# Revit family: Kessel 20223 en
name_source: partatom
category: Sanitärinstallationen
revit_build: Autodesk Revit 2017 (Build: 20160225_1515(x64)
units: mm (PartAtom-declared; Revit-internal decimal feet)

## family parameters
Arbeitsebenenbasiert = Nein
Beim Laden mit Abzugskörper schneiden = Nein
Bemaßung runder Anschluss = Durchmesser verwenden
Gemeinsam genutzt = Nein
Immer vertikal = Ja
Raumberechnungspunkt = Nein
Teiletyp = Normal

## types (1)
- Kessel 20223 en
    <1.010.00.2> Number of the part of the guideline = 4
    <1.010.00.3> Issue date (month) of the guideline = 201410
    <1.010.00.4> Manufacturer name = Kessel
    <1.010.00.5> Revision date of the file = 20190228
    <1.800.00.3> BS number = 10000100000000000000000000000000000000000000000102000
    <1.800.00.4> Comment field = Warngerät mit optischer Sonde
    <1.810.00.3> Manufacturer’s reference number = 20223
    <1.810.00.4> DATANORM number = 20223
    <1.960/3L.00.8> Link (URL) = http://www.kessel.de
    <4.100.00.4> Area of application = Zubehör
    <4.110.00.4> Model series = Zubehör
    <4.700.00.10> Star / delta starting circuit with three-phase connection or three-phase current = no
    <4.700.00.46> vertical installation = no
    <4.700.00.47> outdoor installation = no
    <4.700.00.48> ATEX = no
    <4.700.00.49> protection class = protection class I
    <4.700.00.4> Product name = Warngerät mit optischer Sonde
    <4.700.00.50> motor protection = no
    CONNECTOR0_DIAMETER_dZ_0r = 0 mm  [stored 0 ft]
    CONNECTOR0_dZ_00 = 77 mm
    CONNECTOR0_dZ_01 = 67 mm
    CONNECTOR0_ref_dX = 48 mm
    CONNECTOR0_ref_dY = 22 mm
    CONNECTOR0_ref_dZ = 67 mm
    CONNECTOR1_DIAMETER_dNBN0_0r = 0 mm  [stored 0 ft]
    CONNECTOR1_dNBN0_00 = 76 mm
    CONNECTOR1_dNBN0_01 = 66 mm
    CONNECTOR1_ref_dNBN0 = 66 mm
    CONNECTOR1_ref_dNBN1 = 16 mm
    CONNECTOR1_ref_dY = 22 mm
    CONNECTOR2_DIAMETER_dZ_0r = 0 mm  [stored 0 ft]
    CONNECTOR2_dZ_00 = 73 mm
    CONNECTOR2_dZ_01 = 63 mm
    CONNECTOR2_ref_dNBN0 = 63 mm
    CONNECTOR2_ref_dNBN1 = 16 mm
    CONNECTOR2_ref_dY = 22 mm
    CONNECTOR3_DIAMETER_dZ_0r = 0 mm  [stored 0 ft]
    CONNECTOR3_dZ_00 = 77 mm
    CONNECTOR3_dZ_01 = 67 mm
    CONNECTOR3_ref_dNBN0 = 66 mm
    CONNECTOR3_ref_dNBN1 = 48 mm
    CONNECTOR3_ref_dY = 22 mm
    Hersteller = Kessel
    Modell = 20223
    URL = www.kessel.de

note: [stored X ft] marks values corroborated as IEEE doubles in the binary element streams (Revit-internal decimal feet)

## geometry (parser evidence)
native form markers: Sweep x2
no freeform markers — native parametric forms only
